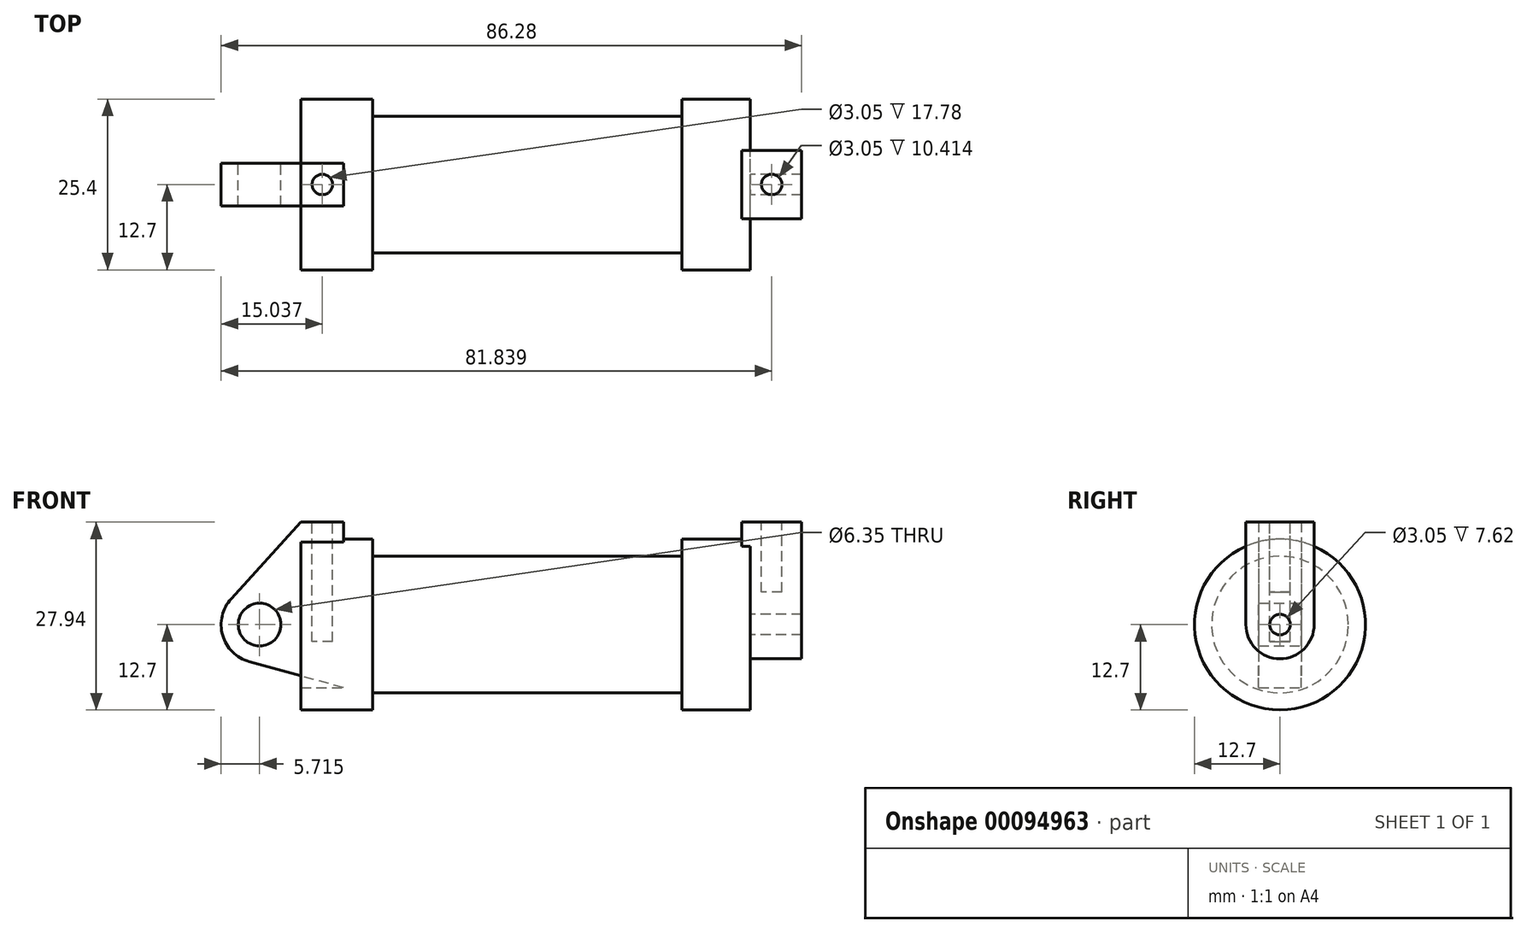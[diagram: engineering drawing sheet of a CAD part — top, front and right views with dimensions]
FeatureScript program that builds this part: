
annotation { "Feature Type Name" : "Feature", "Feature Type Description" : "" }
export const myFeature = defineFeature(function(context is Context, id is Id, definition is map)
    precondition{}
    {
        {
            var Q0;
            Q0=qCreatedBy(makeId("Front.planeOp"),FACE);
            var sketch = newSketch(context, id + "F0", { "sketchPlane" : qUnion([Q0])});
            skLineSegment(sketch, "E0", {"start": v(0, 0) * mm, "end": v(0, 12.7) * mm});
            skLineSegment(sketch, "E1", {"start": v(0, 12.7) * mm, "end": v(10.16, 12.7) * mm});
            skLineSegment(sketch, "E2", {"start": v(10.16, 12.7) * mm, "end": v(10.16, 10.16) * mm});
            skLineSegment(sketch, "E3", {"start": v(10.16, 10.16) * mm, "end": v(56.13, 10.16) * mm});
            skLineSegment(sketch, "E4", {"start": v(56.13, 10.16) * mm, "end": v(56.13, 12.7) * mm});
            skLineSegment(sketch, "E5", {"start": v(56.13, 12.7) * mm, "end": v(66.3, 12.7) * mm});
            skLineSegment(sketch, "E6", {"start": v(66.3, 12.7) * mm, "end": v(66.3, 0) * mm});
            skLineSegment(sketch, "E7", {"start": v(66.3, 0) * mm, "end": v(0, 0) * mm});
            skLineSegment(sketch, "E8", {"start": v(5.84, 15.24) * mm, "end": v(-0.5, 15.24) * mm});
            skLineSegment(sketch, "E9", {"start": v(-0.5, 15.24) * mm, "end": v(-10.88, 3.85) * mm});
            skLineSegment(sketch, "E10", {"start": v(0, 0) * mm, "end": v(-6.65, 0) * mm});
            skCircle(sketch, "E11", {"center": v(-6.65, 0) * mm, "radius": 5.72 * mm});
            skCircle(sketch, "E12", {"center": v(-6.65, 0) * mm, "radius": 3.18 * mm});
            skLineSegment(sketch, "E13", {"start": v(5.84, 15.24) * mm, "end": v(5.84, -9.4) * mm});
            skLineSegment(sketch, "E14", {"start": v(5.84, -9.4) * mm, "end": v(-8.18, -5.5) * mm});
            skSolve(sketch);
        }
        {
            var Q0;
            {var subQ0=sQuery(id+"F0.wireOp",EDGE,"E2");Q0=makeQuery(id+"F0.imprint","IMPRINT",FACE,{"disambiguationData":[TD([[makeQuery(id+"F0.imprint","IMPRINT",EDGE,{"derivedFrom":subQ0}),-1.0]])]});}
            var Q1;
            Q1=sQuery(id+"F0.wireOp",EDGE,"E10");
            revolve(context, id + "F1", {"entities" : qUnion([Q0]), "axis" : qUnion([Q1]), "revolveType" : RevolveType.FULL});
        }
        {
            var Q0;
            {var subQ3=sQuery(id+"F0.wireOp",EDGE,"E0");Q0=makeQuery(id+"F0.imprint","IMPRINT",FACE,{"disambiguationData":[TD([[makeQuery(id+"F0.imprint","IMPRINT",EDGE,{"derivedFrom":subQ3}),1.0]])]});}
            var Q1;
            {var subQ0=sQuery(id+"F0.wireOp",EDGE,"E14");Q1=makeQuery(id+"F0.imprint","IMPRINT",FACE,{"disambiguationData":[TD([[makeQuery(id+"F0.imprint","IMPRINT",EDGE,{"derivedFrom":subQ0}),-1.0]])]});}
            var Q2;
            {var subQ0=sQuery(id+"F0.wireOp",EDGE,"E0");Q2=makeQuery(id+"F0.imprint","IMPRINT",FACE,{"disambiguationData":[TD([[makeQuery(id+"F0.imprint","IMPRINT",EDGE,{"derivedFrom":subQ0}),-1.0]])]});}
            var Q3;
            {var subQ4=sQuery(id+"F0.wireOp",EDGE,"E12");Q3=makeQuery(id+"F0.imprint","IMPRINT",FACE,{"disambiguationData":[TD([[makeQuery(id+"F0.imprint","IMPRINT",EDGE,{"derivedFrom":subQ4}),-1.0]])]});}
            extrude(context, id + "F2", {"entities" : qUnion([Q0, Q1, Q2, Q3]), "operationType" : NewBodyOperationType.ADD, "endBound" : BoundingType.SYMMETRIC, "depth" : 6.35 * mm});
        }
        {
            var Q0;
            Q0=makeQuery(id+"F1.opRevolve","SWEPT_FACE",FACE,{"disambiguationData":[OSD([sQuery(id+"F0.wireOp",EDGE,"E13")])]});
            extrude(context, id + "F3", {"entities" : qUnion([Q0]), "operationType" : NewBodyOperationType.ADD, "depth" : 6.35 * mm});
        }
        {
            var Q0;
            Q0=makeQuery(id+"F1.opRevolve","SWEPT_FACE",FACE,{"disambiguationData":[OSD([sQuery(id+"F0.wireOp",EDGE,"E6")])]});
            var sketch = newSketch(context, id + "F4", { "sketchPlane" : qUnion([Q0])});
            skCircle(sketch, "E15", {"center": v(0, 0) * mm, "radius": 1.52 * mm});
            skCircle(sketch, "E16", {"center": v(0, 0) * mm, "radius": 5.08 * mm});
            skLineSegment(sketch, "E17", {"start": v(5.08, 0) * mm, "end": v(5.08, 15.24) * mm});
            skLineSegment(sketch, "E18", {"start": v(-5.08, 0) * mm, "end": v(-5.08, 15.24) * mm});
            skLineSegment(sketch, "E19", {"start": v(-5.08, 15.24) * mm, "end": v(5.08, 15.24) * mm});
            skSolve(sketch);
        }
        {
            var Q0;
            {var subQ0=sQuery(id+"F4.wireOp",EDGE,"E17");var subQ1=sQuery(id+"F4.wireOp",EDGE,"E16");var subQ2=makeQuery(id+"F4.imprint","INTERSECT",VERTEX,{"derivedFrom":[subQ1,subQ0]});Q0=makeQuery(id+"F4.imprint","IMPRINT",FACE,{"disambiguationData":[TD([[makeQuery(id+"F4.imprint","IMPRINT",EDGE,{"disambiguationData":[TD([[subQ2,-1.0]])],"derivedFrom":subQ1}),-1.0]])]});}
            var Q1;
            Q1=makeQuery(id+"F4.imprint","IMPRINT",FACE,{"disambiguationData":[TD([[makeQuery(id+"F4.imprint","IMPRINT",EDGE,{"derivedFrom":sQuery(id+"F4.wireOp",EDGE,"E15")}),-1.0]])]});
            var Q2;
            {var subQ0=sQuery(id+"F4.wireOp",EDGE,"E19");Q2=makeQuery(id+"F4.imprint","IMPRINT",FACE,{"disambiguationData":[TD([[makeQuery(id+"F4.imprint","IMPRINT",EDGE,{"derivedFrom":subQ0}),-1.0]])]});}
            extrude(context, id + "F5", {"entities" : qUnion([Q0, Q1, Q2]), "operationType" : NewBodyOperationType.ADD, "depth" : 7.62 * mm});
        }
        {
            var Q0;
            Q0=makeQuery(id+"F5.opExtrude","CAP_FACE",FACE,{"disambiguationData":[OSD([sQuery(id+"F4.wireOp",EDGE,"E15"),sQuery(id+"F4.wireOp",EDGE,"E16"),sQuery(id+"F4.wireOp",EDGE,"E17"),sQuery(id+"F4.wireOp",EDGE,"E18"),sQuery(id+"F4.wireOp",EDGE,"E19")])],"isStart":true});
            extrude(context, id + "F6", {"entities" : qUnion([Q0]), "operationType" : NewBodyOperationType.ADD, "depth" : 1.27 * mm});
        }
        {
            var Q0;
            Q0=makeQuery(id+"F2.opExtrude","SWEPT_FACE",FACE,{"disambiguationData":[OSD([sQuery(id+"F0.wireOp",EDGE,"E8")])]});
            var sketch = newSketch(context, id + "F7", { "sketchPlane" : qUnion([Q0])});
            skCircle(sketch, "E20", {"center": v(2.67, 0) * mm, "radius": 1.52 * mm});
            skSolve(sketch);
        }
        {
            var Q0;
            Q0=makeQuery(id+"F7.imprint","IMPRINT",FACE,{"disambiguationData":[TD([[makeQuery(id+"F7.imprint","IMPRINT",EDGE,{"derivedFrom":sQuery(id+"F7.wireOp",EDGE,"E20")}),1.0]])]});
            extrude(context, id + "F8", {"entities" : qUnion([Q0]), "operationType" : NewBodyOperationType.REMOVE, "oppositeDirection" : true, "depth" : 17.78 * mm});
        }
        {
            var Q0;
            {var subQ0=sQuery(id+"F4.wireOp",EDGE,"E19");Q0=makeQuery(id+"F6.boolean.opBoolean","MERGE",FACE,{"derivedFrom":[makeQuery(id+"F5.opExtrude","SWEPT_FACE",FACE,{"disambiguationData":[OSD([subQ0])]}),makeQuery(id+"F6.opExtrude","SWEPT_FACE",FACE,{"disambiguationData":[OSD([subQ0])]})]});}
            var sketch = newSketch(context, id + "F9", { "sketchPlane" : qUnion([Q0])});
            skCircle(sketch, "E21", {"center": v(69.47, 0) * mm, "radius": 1.52 * mm});
            skSolve(sketch);
        }
        {
            var Q0;
            Q0=makeQuery(id+"F9.imprint","IMPRINT",FACE,{"disambiguationData":[TD([[makeQuery(id+"F9.imprint","IMPRINT",EDGE,{"derivedFrom":sQuery(id+"F9.wireOp",EDGE,"E21")}),1.0]])]});
            extrude(context, id + "F10", {"entities" : qUnion([Q0]), "operationType" : NewBodyOperationType.REMOVE, "oppositeDirection" : true, "depth" : 10.4 * mm});
        }
    });
